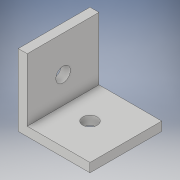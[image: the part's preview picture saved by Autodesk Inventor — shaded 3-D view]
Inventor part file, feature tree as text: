
AUTODESK INVENTOR PART (.ipt)
format: ipt  version: 2018 (Build 220112000, 112)  size: 112,640 bytes
history: native  units: in
note: dims shown in document units (in); Inventor stores cm internally (conversion verified against a paired STEP export)
features: extrude x3, sketch x3
ambient origin geometry x8: Origin, YZ Plane, XZ Plane, XY Plane, X Axis, Y Axis, Z Axis, Center Point
bodies: Solid1 (feature_tree)
feature tree (6):
  extrude  "Extrusion1"  Depth=1.0in
  extrude  "Extrusion2"  Depth=0.125in
  extrude  "Extrusion3"  Depth=1.0in
  sketch  "Sketch1"  dims[d0=0.125in d1=1.0in]
  sketch  "Sketch2"  dims[d2=1.0in d3=0.125in]
  sketch  "Sketch3"  dims[d4=1.0in d5=0.0in d6=0.5in d7=0.2031in d8=1.0in d9=0.0in d10=0.5in d11=0.2031in d12=1.0in d13=0.0in]
